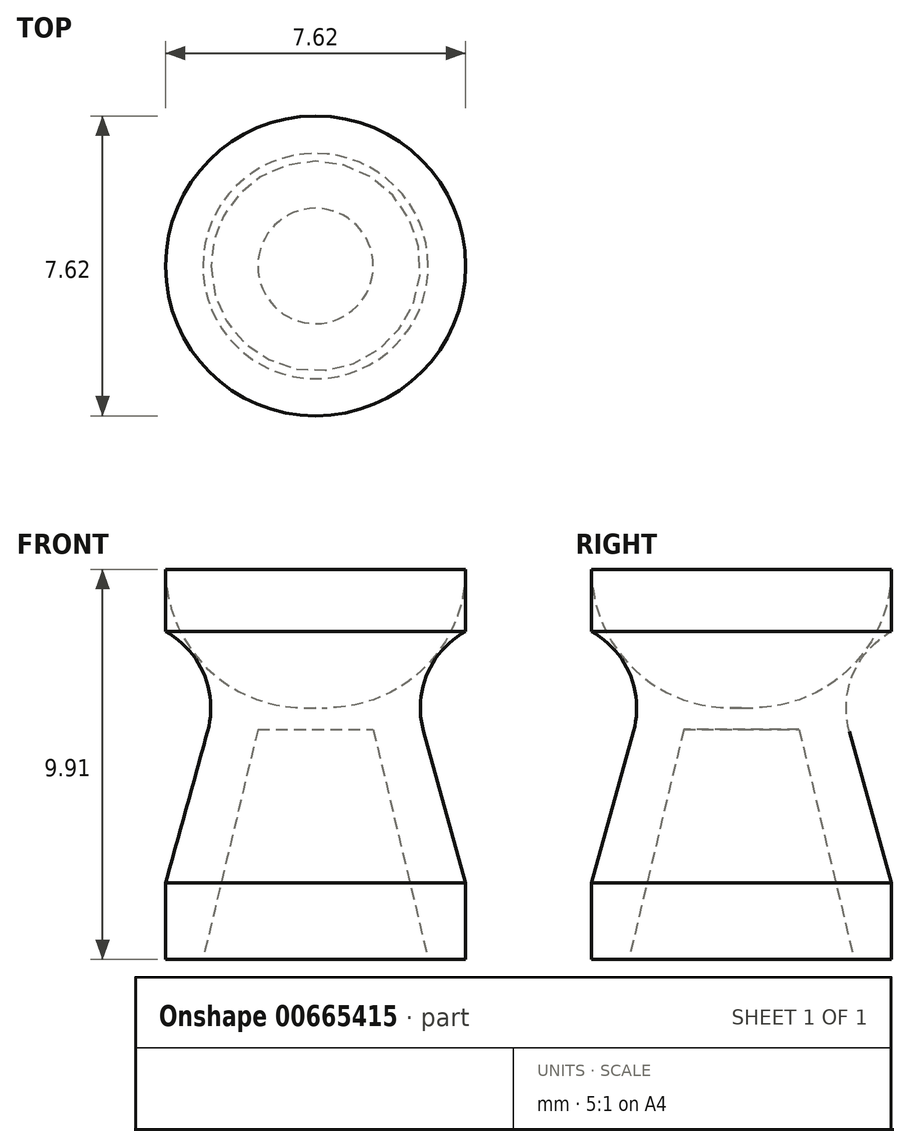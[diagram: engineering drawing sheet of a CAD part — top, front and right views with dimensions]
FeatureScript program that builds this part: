
annotation { "Feature Type Name" : "Feature", "Feature Type Description" : "" }
export const myFeature = defineFeature(function(context is Context, id is Id, definition is map)
    precondition{}
    {
        {
            var Q0;
            Q0=qCreatedBy(makeId("Front.planeOp"),FACE);
            var sketch = newSketch(context, id + "F0", { "sketchPlane" : qUnion([Q0])});
            skLineSegment(sketch, "E0", {"start": v(3.81, 9.91) * mm, "end": v(3.81, 8.33) * mm});
            skArc(sketch, "E1", {"start": v(3.81, 9.91) * mm, "mid": v(2.67, 12.5) * mm, "end": v(0, 13.42) * mm});
            skLineSegment(sketch, "E2", {"start": v(3.81, 0) * mm, "end": v(3.81, 1.95) * mm});
            skLineSegment(sketch, "E3", {"start": v(3.81, 1.95) * mm, "end": v(2.74, 5.8) * mm});
            skArc(sketch, "E4", {"start": v(3.81, 8.33) * mm, "mid": v(2.83, 7.25) * mm, "end": v(2.74, 5.8) * mm});
            skLineSegment(sketch, "E5", {"start": v(3.81, 0) * mm, "end": v(2.86, 0) * mm});
            skLineSegment(sketch, "E6", {"start": v(2.86, 0) * mm, "end": v(1.47, 5.85) * mm});
            skLineSegment(sketch, "E7", {"start": v(1.47, 5.85) * mm, "end": v(0, 5.85) * mm});
            skPoint(sketch, "E8.orphan", {"position": v(0, 0) * mm});
            skPoint(sketch, "E9.end.orphan", {"position": v(0, 9.91) * mm});
            skLineSegment(sketch, "E10", {"start": v(0, 5.85) * mm, "end": v(0, 13.42) * mm});
            skSolve(sketch);
        }
        {
            var Q0;
            Q0=makeQuery(id+"F0.imprint","IMPRINT",FACE,{"disambiguationData":[TD([[makeQuery(id+"F0.imprint","IMPRINT",EDGE,{"derivedFrom":sQuery(id+"F0.wireOp",EDGE,"E0")}),-1.0]])]});
            var Q1;
            Q1=sQuery(id+"F0.wireOp",EDGE,"E10");
            revolve(context, id + "F1", {"surfaceOperationType" : NewSurfaceOperationType.NEW, "entities" : qUnion([Q0]), "axis" : qUnion([Q1]), "revolveType" : RevolveType.FULL});
        }
    });
